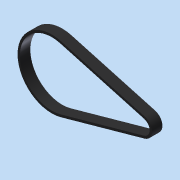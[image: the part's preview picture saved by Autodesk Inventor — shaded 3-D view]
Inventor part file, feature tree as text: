
AUTODESK INVENTOR PART (.ipt)
format: ipt  version: 2015 (Build 190159000, 159)  size: 235,008 bytes
history: native  units: in
note: dims shown in document units (in); Inventor stores cm internally (conversion verified against a paired STEP export)
features: other x4, extrude x1, sketch x1
ambient origin geometry x8: Origin, YZ Plane, XZ Plane, XY Plane, X Axis, Y Axis, Z Axis, Center Point
bodies: Body1 (feature_tree), Body2 (feature_tree)
feature tree (6):
  other  "MotorMount.ipt"
  extrude  "Extrusion2"  Depth=0.3937in
  other  "TaggingFeature1"
  sketch  "Sketch2"  dims[d23=0.3937in d24=2.3307in d25=0.6772in d26=0.0787in d27=0.3543in d28=0.0in]
  other  "Solid2::MotorMount.ipt"
  other  "Srf1"
